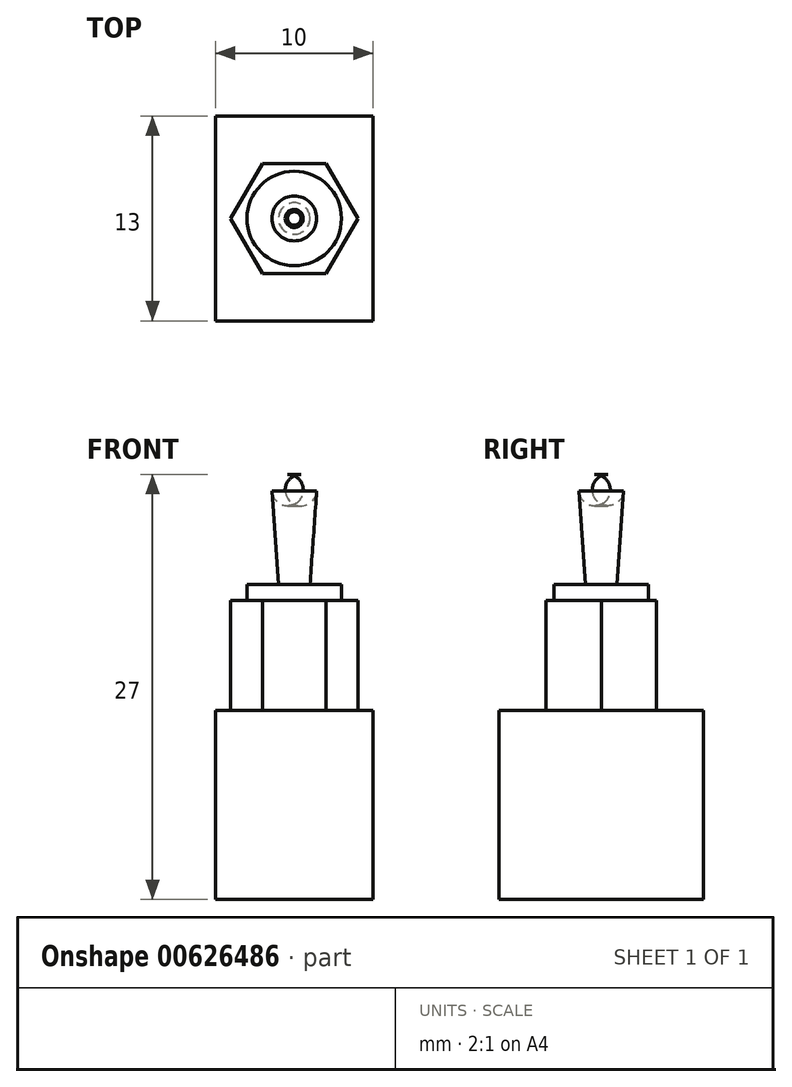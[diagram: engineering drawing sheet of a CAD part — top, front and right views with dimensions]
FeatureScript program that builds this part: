
annotation { "Feature Type Name" : "Feature", "Feature Type Description" : "" }
export const myFeature = defineFeature(function(context is Context, id is Id, definition is map)
    precondition{}
    {
        {
            var Q0;
            Q0=qCreatedBy(makeId("Top.planeOp"),FACE);
            var sketch = newSketch(context, id + "F0", { "sketchPlane" : qUnion([Q0])});
            skLineSegment(sketch, "E0.bottom", {"start": v(5, -6.5) * mm, "end": v(-5, -6.5) * mm});
            skLineSegment(sketch, "E0.top", {"start": v(5, 6.5) * mm, "end": v(-5, 6.5) * mm});
            skLineSegment(sketch, "E0.left", {"start": v(5, -6.5) * mm, "end": v(5, 6.5) * mm});
            skLineSegment(sketch, "E0.right", {"start": v(-5, -6.5) * mm, "end": v(-5, 6.5) * mm});
            skPoint(sketch, "E0.middle", {"position": v(0, 0) * mm});
            skCircle(sketch, "E1.cCircle", {"center": v(0, 0) * mm, "radius": 3.5 * mm, "construction": true});
            skLineSegment(sketch, "E1.0", {"start": v(2.02, -3.5) * mm, "end": v(-2.02, -3.5) * mm});
            skLineSegment(sketch, "E1.1", {"start": v(-2.02, -3.5) * mm, "end": v(-4.04, 0) * mm});
            skLineSegment(sketch, "E1.2", {"start": v(-4.04, 0) * mm, "end": v(-2.02, 3.5) * mm});
            skLineSegment(sketch, "E1.3", {"start": v(-2.02, 3.5) * mm, "end": v(2.02, 3.5) * mm});
            skLineSegment(sketch, "E1.4", {"start": v(2.02, 3.5) * mm, "end": v(4.04, 0) * mm});
            skLineSegment(sketch, "E1.5", {"start": v(4.04, 0) * mm, "end": v(2.02, -3.5) * mm});
            skPoint(sketch, "E1.0.midPoint", {"position": v(0, -3.5) * mm});
            skSolve(sketch);
        }
        {
            var Q0;
            Q0=makeQuery(id+"F0.imprint","IMPRINT",FACE,{"disambiguationData":[TD([[makeQuery(id+"F0.imprint","IMPRINT",EDGE,{"derivedFrom":sQuery(id+"F0.wireOp",EDGE,"E0.bottom")}),-1.0]])]});
            var Q1;
            Q1=makeQuery(id+"F0.imprint","IMPRINT",FACE,{"disambiguationData":[TD([[makeQuery(id+"F0.imprint","IMPRINT",EDGE,{"derivedFrom":sQuery(id+"F0.wireOp",EDGE,"E1.0")}),-1.0]])]});
            extrude(context, id + "F1", {"entities" : qUnion([Q0, Q1]), "oppositeDirection" : true, "depth" : 12 * mm, "offsetDistance" : 25 * mm});
        }
        {
            var Q0;
            Q0=makeQuery(id+"F0.imprint","IMPRINT",FACE,{"disambiguationData":[TD([[makeQuery(id+"F0.imprint","IMPRINT",EDGE,{"derivedFrom":sQuery(id+"F0.wireOp",EDGE,"E1.0")}),-1.0]])]});
            extrude(context, id + "F2", {"entities" : qUnion([Q0]), "operationType" : NewBodyOperationType.ADD, "depth" : 7 * mm, "offsetDistance" : 25 * mm});
        }
        {
            var Q0;
            Q0=makeQuery(id+"F2.opExtrude","CAP_FACE",FACE,{"disambiguationData":[OSD([sQuery(id+"F0.wireOp",EDGE,"E1.0"),sQuery(id+"F0.wireOp",EDGE,"E1.1"),sQuery(id+"F0.wireOp",EDGE,"E1.2"),sQuery(id+"F0.wireOp",EDGE,"E1.3"),sQuery(id+"F0.wireOp",EDGE,"E1.4"),sQuery(id+"F0.wireOp",EDGE,"E1.5")])],"isStart":false});
            var sketch = newSketch(context, id + "F3", { "sketchPlane" : qUnion([Q0])});
            skCircle(sketch, "E2", {"center": v(0, 0) * mm, "radius": 3 * mm});
            skSolve(sketch);
        }
        {
            var Q0;
            Q0=makeQuery(id+"F3.imprint","IMPRINT",FACE,{"disambiguationData":[TD([[makeQuery(id+"F3.imprint","IMPRINT",EDGE,{"derivedFrom":sQuery(id+"F3.wireOp",EDGE,"E2")}),1.0]])]});
            extrude(context, id + "F4", {"entities" : qUnion([Q0]), "operationType" : NewBodyOperationType.ADD, "depth" : 1 * mm, "offsetDistance" : 25 * mm});
        }
        {
            var Q0;
            Q0=makeQuery(id+"F4.opExtrude","CAP_FACE",FACE,{"disambiguationData":[OSD([sQuery(id+"F3.wireOp",EDGE,"E2")])],"isStart":false});
            var sketch = newSketch(context, id + "F5", { "sketchPlane" : qUnion([Q0])});
            skCircle(sketch, "E3", {"center": v(0, 0) * mm, "radius": 1 * mm});
            skSolve(sketch);
        }
        {
            var Q0;
            Q0=makeQuery(id+"F5.imprint","IMPRINT",FACE,{"disambiguationData":[TD([[makeQuery(id+"F5.imprint","IMPRINT",EDGE,{"derivedFrom":sQuery(id+"F5.wireOp",EDGE,"E3")}),-1.0]])]});
            cPlane(context, id + "F6", {"entities" : qUnion([Q0]), "cplaneType" : CPlaneType.OFFSET, "offset" : 7 * mm, "width" : 150 * mm, "height" : 150 * mm});
        }
        {
            var Q0;
            Q0=qCreatedBy(id+"F6.planeOp",FACE);
            var sketch = newSketch(context, id + "F7", { "sketchPlane" : qUnion([Q0])});
            skCircle(sketch, "E4", {"center": v(0, 0) * mm, "radius": 1.5 * mm});
            skSolve(sketch);
        }
        {
            var Q1;
            Q1=makeQuery(id+"F5.imprint","IMPRINT",FACE,{"disambiguationData":[TD([[makeQuery(id+"F5.imprint","IMPRINT",EDGE,{"derivedFrom":sQuery(id+"F5.wireOp",EDGE,"E3")}),1.0]])]});
            var Q2;
            Q2=makeQuery(id+"F7.imprint","IMPRINT",FACE,{"disambiguationData":[TD([[makeQuery(id+"F7.imprint","IMPRINT",EDGE,{"derivedFrom":sQuery(id+"F7.wireOp",EDGE,"E4")}),1.0]])]});
            loft(context, id + "F8", {"sheetProfilesArray" : [{ "sheetProfileEntities" : qUnion([Q1]) }, { "sheetProfileEntities" : qUnion([Q2]) }]});
        }
        {
            var Q0;
            Q0=makeQuery(id+"F8.opLoft","MID_CAP_EDGE",EDGE,{"disambiguationData":[OSD([sQuery(id+"F5.wireOp",EDGE,"E3"),sQuery(id+"F7.wireOp",EDGE,"E4")])],"capPos":1.0});
            fillet(context, id + "F9", {"entities" : qUnion([Q0]), "radius" : 1 * mm, "tangentPropagation" : true, "allowEdgeOverflow" : false});
        }
    });
